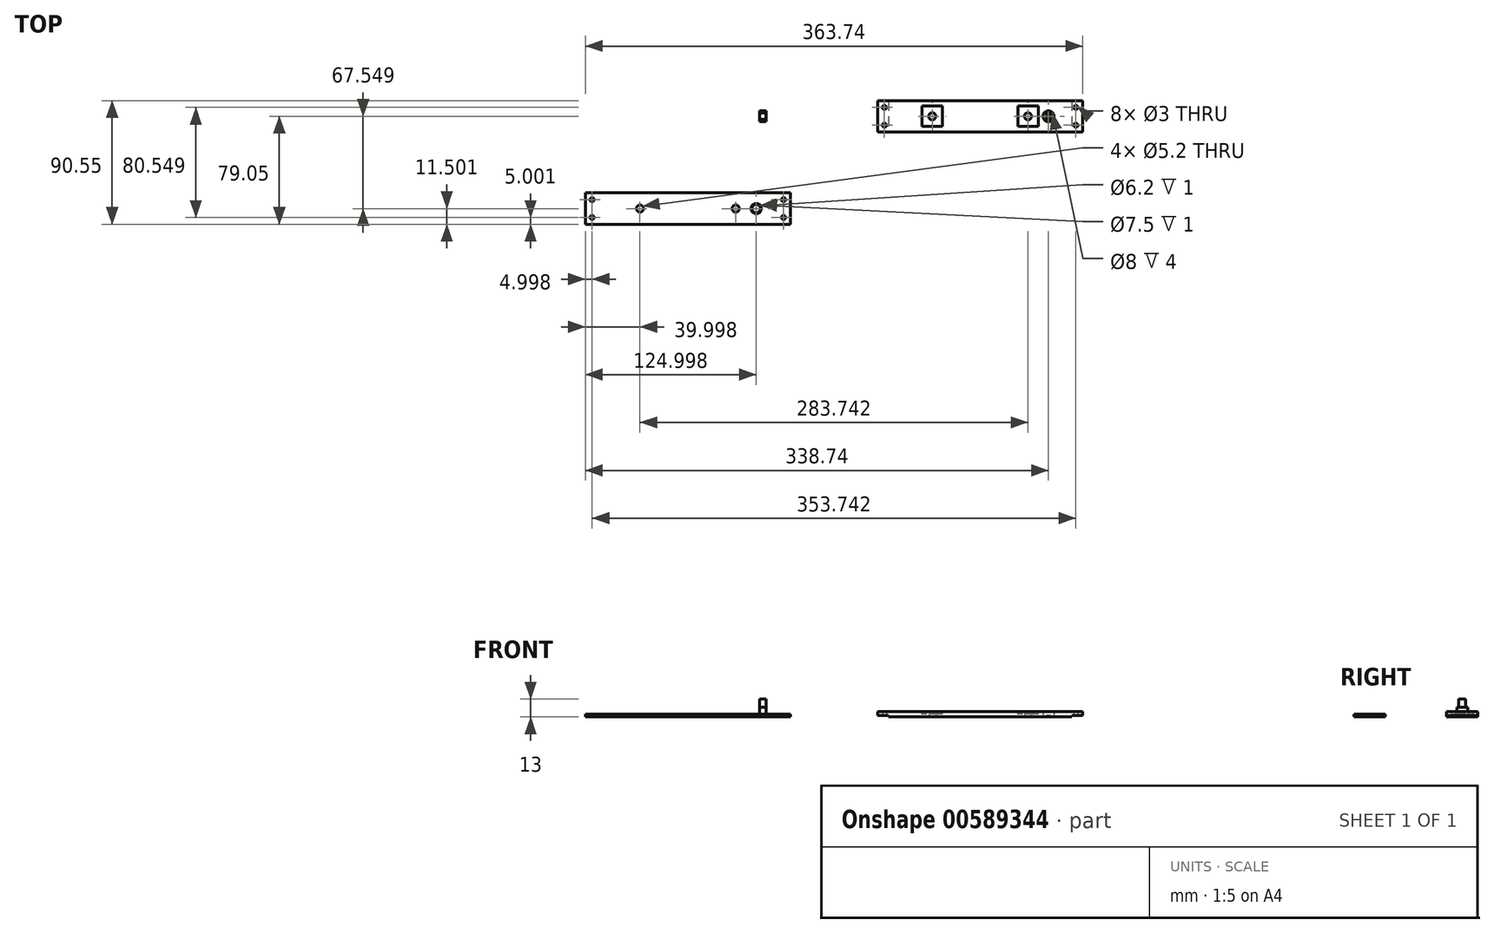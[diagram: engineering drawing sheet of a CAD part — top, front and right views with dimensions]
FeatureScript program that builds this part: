
annotation { "Feature Type Name" : "Feature", "Feature Type Description" : "" }
export const myFeature = defineFeature(function(context is Context, id is Id, definition is map)
    precondition{}
    {
        {
            var Q0;
            Q0=qCreatedBy(makeId("Top.planeOp"),FACE);
            var sketch = newSketch(context, id + "F0", { "sketchPlane" : qUnion([Q0])});
            skLineSegment(sketch, "E0.bottom", {"start": v(75, -11.5) * mm, "end": v(-75, -11.5) * mm});
            skLineSegment(sketch, "E0.top", {"start": v(75, 11.5) * mm, "end": v(-75, 11.5) * mm});
            skLineSegment(sketch, "E0.left", {"start": v(75, -11.5) * mm, "end": v(75, 11.5) * mm});
            skLineSegment(sketch, "E0.right", {"start": v(-75, -11.5) * mm, "end": v(-75, 11.5) * mm});
            skPoint(sketch, "E0.middle", {"position": v(0, 0) * mm});
            skLineSegment(sketch, "E1.bottom", {"start": v(-75, 11.5) * mm, "end": v(-67, 11.5) * mm, "construction": true});
            skLineSegment(sketch, "E1.top", {"start": v(-75, -11.5) * mm, "end": v(-67, -11.5) * mm, "construction": true});
            skLineSegment(sketch, "E1.left", {"start": v(-75, 11.5) * mm, "end": v(-75, -11.5) * mm, "construction": true});
            skLineSegment(sketch, "E1.right", {"start": v(-67, 11.5) * mm, "end": v(-67, -11.5) * mm, "construction": true});
            skLineSegment(sketch, "E2.bottom", {"start": v(75, -11.5) * mm, "end": v(67, -11.5) * mm, "construction": true});
            skLineSegment(sketch, "E2.top", {"start": v(75, 11.5) * mm, "end": v(67, 11.5) * mm, "construction": true});
            skLineSegment(sketch, "E2.left", {"start": v(75, -11.5) * mm, "end": v(75, 11.5) * mm, "construction": true});
            skLineSegment(sketch, "E2.right", {"start": v(67, -11.5) * mm, "end": v(67, 11.5) * mm, "construction": true});
            skCircle(sketch, "E3", {"center": v(-35, 0) * mm, "radius": 2.6 * mm});
            skCircle(sketch, "E4", {"center": v(35, 0) * mm, "radius": 2.6 * mm});
            skCircle(sketch, "E5", {"center": v(50, 0) * mm, "radius": 4 * mm});
            skLineSegment(sketch, "E6.left", {"start": v(51.5, -3.7) * mm, "end": v(51.5, 3.7) * mm});
            skLineSegment(sketch, "E6.right", {"start": v(48.5, -3.7) * mm, "end": v(48.5, 3.7) * mm});
            skCircle(sketch, "E7", {"center": v(-70, 6.5) * mm, "radius": 1.5 * mm});
            skCircle(sketch, "E8", {"center": v(-70, -6.5) * mm, "radius": 1.5 * mm});
            skCircle(sketch, "E9", {"center": v(70, 6.5) * mm, "radius": 1.5 * mm});
            skCircle(sketch, "E10", {"center": v(70, -6.5) * mm, "radius": 1.5 * mm});
            skSolve(sketch);
        }
        {
            var Q0;
            Q0=qCreatedBy(makeId("Top.planeOp"),FACE);
            var sketch = newSketch(context, id + "F1", { "sketchPlane" : qUnion([Q0])});
            skLineSegment(sketch, "E11.bottom", {"start": v(-156.38, -3.9) * mm, "end": v(-161.38, -3.9) * mm});
            skLineSegment(sketch, "E11.top", {"start": v(-156.38, 4.1) * mm, "end": v(-161.38, 4.1) * mm});
            skLineSegment(sketch, "E11.left", {"start": v(-156.38, -3.9) * mm, "end": v(-156.38, 4.1) * mm});
            skLineSegment(sketch, "E11.right", {"start": v(-161.38, -3.9) * mm, "end": v(-161.38, 4.1) * mm});
            skPoint(sketch, "E11.middle", {"position": v(-158.88, 0.1) * mm});
            skSolve(sketch);
        }
        {
            var Q0;
            Q0=makeQuery(id+"F1.imprint","IMPRINT",FACE,{"disambiguationData":[TD([[makeQuery(id+"F1.imprint","IMPRINT",EDGE,{"derivedFrom":sQuery(id+"F1.wireOp",EDGE,"E11.bottom")}),-1.0]])]});
            extrude(context, id + "F2", {"entities" : qUnion([Q0]), "depth" : 7 * mm});
        }
        {
            var Q0;
            Q0=makeQuery(id+"F2.opExtrude","CAP_FACE",FACE,{"disambiguationData":[OSD([sQuery(id+"F1.wireOp",EDGE,"E11.bottom"),sQuery(id+"F1.wireOp",EDGE,"E11.top"),sQuery(id+"F1.wireOp",EDGE,"E11.left"),sQuery(id+"F1.wireOp",EDGE,"E11.right")])],"isStart":false});
            var sketch = newSketch(context, id + "F3", { "sketchPlane" : qUnion([Q0])});
            skCircle(sketch, "E12", {"center": v(-158.88, 0.1) * mm, "radius": 2.5 * mm});
            skPoint(sketch, "E12.centerSnap0", {"position": v(-161.38, 0.1) * mm});
            skPoint(sketch, "E12.centerSnap1", {"position": v(-158.88, 4.1) * mm});
            skSolve(sketch);
        }
        {
            var Q0;
            {var subQ0=sQuery(id+"F3.wireOp",EDGE,"E12");var subQ1=makeQuery(id+"F3.imprint","INTERSECT",VERTEX,{"derivedFrom":[makeQuery(id+"F2.opExtrude","CAP_EDGE",EDGE,{"disambiguationData":[OSD([sQuery(id+"F1.wireOp",EDGE,"E11.left")])],"isStart":false}),subQ0]});Q0=makeQuery(id+"F3.imprint","IMPRINT",FACE,{"disambiguationData":[TD([[makeQuery(id+"F3.imprint","IMPRINT",EDGE,{"disambiguationData":[TD([[subQ1,-1.0]])],"derivedFrom":subQ0}),1.0]])]});}
            extrude(context, id + "F4", {"entities" : qUnion([Q0]), "operationType" : NewBodyOperationType.ADD, "depth" : 6 * mm});
        }
        {
            var Q0;
            Q0=makeQuery(id+"F0.imprint","IMPRINT",FACE,{"disambiguationData":[TD([[makeQuery(id+"F0.imprint","IMPRINT",EDGE,{"derivedFrom":sQuery(id+"F0.wireOp",EDGE,"E0.bottom")}),-1.0]])]});
            var Q1;
            {var subQ0=sQuery(id+"F0.wireOp",EDGE,"E6.left");Q1=makeQuery(id+"F0.imprint","IMPRINT",FACE,{"disambiguationData":[TD([[makeQuery(id+"F0.imprint","IMPRINT",EDGE,{"derivedFrom":subQ0}),1.0]])]});}
            extrude(context, id + "F5", {"entities" : qUnion([Q0, Q1]), "depth" : 4 * mm});
        }
        {
            var Q0;
            Q0=qCreatedBy(makeId("Top.planeOp"),FACE);
            var sketch = newSketch(context, id + "F6", { "sketchPlane" : qUnion([Q0])});
            skLineSegment(sketch, "E13.bottom", {"start": v(-138.74, -79.05) * mm, "end": v(-288.74, -79.05) * mm});
            skLineSegment(sketch, "E13.top", {"start": v(-138.74, -56.05) * mm, "end": v(-288.74, -56.05) * mm});
            skLineSegment(sketch, "E13.left", {"start": v(-138.74, -79.05) * mm, "end": v(-138.74, -56.05) * mm});
            skLineSegment(sketch, "E13.right", {"start": v(-288.74, -79.05) * mm, "end": v(-288.74, -56.05) * mm});
            skPoint(sketch, "E13.middle", {"position": v(-213.74, -67.55) * mm});
            skLineSegment(sketch, "E14.bottom", {"start": v(-288.74, -56.05) * mm, "end": v(-280.74, -56.05) * mm, "construction": true});
            skLineSegment(sketch, "E14.top", {"start": v(-288.74, -79.05) * mm, "end": v(-280.74, -79.05) * mm, "construction": true});
            skLineSegment(sketch, "E14.left", {"start": v(-288.74, -56.05) * mm, "end": v(-288.74, -79.05) * mm, "construction": true});
            skLineSegment(sketch, "E14.right", {"start": v(-280.74, -56.05) * mm, "end": v(-280.74, -79.05) * mm, "construction": true});
            skLineSegment(sketch, "E15.bottom", {"start": v(-138.74, -79.05) * mm, "end": v(-146.74, -79.05) * mm, "construction": true});
            skLineSegment(sketch, "E15.top", {"start": v(-138.74, -56.05) * mm, "end": v(-146.74, -56.05) * mm, "construction": true});
            skLineSegment(sketch, "E15.left", {"start": v(-138.74, -79.05) * mm, "end": v(-138.74, -56.05) * mm, "construction": true});
            skLineSegment(sketch, "E15.right", {"start": v(-146.74, -79.05) * mm, "end": v(-146.74, -56.05) * mm, "construction": true});
            skCircle(sketch, "E16", {"center": v(-248.74, -67.55) * mm, "radius": 2.6 * mm});
            skCircle(sketch, "E17", {"center": v(-178.74, -67.55) * mm, "radius": 2.6 * mm});
            skCircle(sketch, "E18", {"center": v(-163.74, -67.55) * mm, "radius": 3.1 * mm});
            skCircle(sketch, "E19", {"center": v(-283.74, -61.05) * mm, "radius": 1.5 * mm});
            skCircle(sketch, "E20", {"center": v(-283.74, -74.05) * mm, "radius": 1.5 * mm});
            skCircle(sketch, "E21", {"center": v(-143.74, -61.05) * mm, "radius": 1.5 * mm});
            skCircle(sketch, "E22", {"center": v(-143.74, -74.05) * mm, "radius": 1.5 * mm});
            skSolve(sketch);
        }
        {
            var Q0;
            Q0=makeQuery(id+"F6.imprint","IMPRINT",FACE,{"disambiguationData":[TD([[makeQuery(id+"F6.imprint","IMPRINT",EDGE,{"derivedFrom":sQuery(id+"F6.wireOp",EDGE,"E13.bottom")}),-1.0]])]});
            extrude(context, id + "F7", {"entities" : qUnion([Q0]), "depth" : 2 * mm});
        }
        {
            var Q0;
            Q0=makeQuery(id+"F7.opExtrude","CAP_FACE",FACE,{"disambiguationData":[OSD([sQuery(id+"F6.wireOp",EDGE,"E13.bottom"),sQuery(id+"F6.wireOp",EDGE,"E13.top"),sQuery(id+"F6.wireOp",EDGE,"E13.left"),sQuery(id+"F6.wireOp",EDGE,"E13.right"),sQuery(id+"F6.wireOp",EDGE,"E16"),sQuery(id+"F6.wireOp",EDGE,"E17"),sQuery(id+"F6.wireOp",EDGE,"E18")])],"isStart":false});
            var sketch = newSketch(context, id + "F8", { "sketchPlane" : qUnion([Q0])});
            skCircle(sketch, "E23", {"center": v(-163.74, -67.55) * mm, "radius": 3.75 * mm});
            skSolve(sketch);
        }
        {
            var Q0;
            Q0=qSketchRegion(id+"F8",true);
            extrude(context, id + "F9", {"entities" : qUnion([Q0]), "operationType" : NewBodyOperationType.REMOVE, "oppositeDirection" : true, "depth" : 1 * mm});
        }
        {
            var Q0;
            Q0=makeQuery(id+"F5.opExtrude","SWEPT_FACE",FACE,{"disambiguationData":[OSD([sQuery(id+"F0.wireOp",EDGE,"E0.bottom")])]});
            var sketch = newSketch(context, id + "F10", { "sketchPlane" : qUnion([Q0])});
            skLineSegment(sketch, "E24.bottom", {"start": v(-75, 0) * mm, "end": v(-67, 0) * mm});
            skLineSegment(sketch, "E24.top", {"start": v(-75, 1) * mm, "end": v(-67, 1) * mm});
            skLineSegment(sketch, "E24.left", {"start": v(-75, 0) * mm, "end": v(-75, 1) * mm});
            skLineSegment(sketch, "E24.right", {"start": v(-67, 0) * mm, "end": v(-67, 1) * mm});
            skLineSegment(sketch, "E25.bottom", {"start": v(75, 0) * mm, "end": v(67, 0) * mm});
            skLineSegment(sketch, "E25.top", {"start": v(75, 1) * mm, "end": v(67, 1) * mm});
            skLineSegment(sketch, "E25.left", {"start": v(75, 0) * mm, "end": v(75, 1) * mm});
            skLineSegment(sketch, "E25.right", {"start": v(67, 0) * mm, "end": v(67, 1) * mm});
            skSolve(sketch);
        }
        {
            var Q0;
            Q0=qSketchRegion(id+"F10",true);
            extrude(context, id + "F11", {"entities" : qUnion([Q0]), "operationType" : NewBodyOperationType.REMOVE, "oppositeDirection" : true, "depth" : 30 * mm});
        }
        {
            var Q0;
            Q0=makeQuery(id+"F5.opExtrude","CAP_FACE",FACE,{"disambiguationData":[OSD([sQuery(id+"F0.wireOp",EDGE,"E0.bottom"),sQuery(id+"F0.wireOp",EDGE,"E0.top"),sQuery(id+"F0.wireOp",EDGE,"E0.left"),sQuery(id+"F0.wireOp",EDGE,"E0.right"),sQuery(id+"F0.wireOp",EDGE,"E3"),sQuery(id+"F0.wireOp",EDGE,"E4"),sQuery(id+"F0.wireOp",EDGE,"E5")])],"isStart":false});
            var sketch = newSketch(context, id + "F12", { "sketchPlane" : qUnion([Q0])});
            skLineSegment(sketch, "E26.bottom", {"start": v(-27.5, -7.5) * mm, "end": v(-42.5, -7.5) * mm});
            skLineSegment(sketch, "E26.top", {"start": v(-27.5, 7.5) * mm, "end": v(-42.5, 7.5) * mm});
            skLineSegment(sketch, "E26.left", {"start": v(-27.5, -7.5) * mm, "end": v(-27.5, 7.5) * mm});
            skLineSegment(sketch, "E26.right", {"start": v(-42.5, -7.5) * mm, "end": v(-42.5, 7.5) * mm});
            skPoint(sketch, "E26.middle", {"position": v(-35, 0) * mm});
            skLineSegment(sketch, "E27.bottom", {"start": v(42.5, -7.5) * mm, "end": v(27.5, -7.5) * mm});
            skLineSegment(sketch, "E27.top", {"start": v(42.5, 7.5) * mm, "end": v(27.5, 7.5) * mm});
            skLineSegment(sketch, "E27.left", {"start": v(42.5, -7.5) * mm, "end": v(42.5, 7.5) * mm});
            skLineSegment(sketch, "E27.right", {"start": v(27.5, -7.5) * mm, "end": v(27.5, 7.5) * mm});
            skPoint(sketch, "E27.middle", {"position": v(35, 0) * mm});
            skSolve(sketch);
        }
        {
            var Q0;
            Q0=makeQuery(id+"F12.imprint","IMPRINT",FACE,{"disambiguationData":[TD([[makeQuery(id+"F12.imprint","IMPRINT",EDGE,{"derivedFrom":sQuery(id+"F12.wireOp",EDGE,"E26.bottom")}),-1.0]])]});
            var Q1;
            Q1=makeQuery(id+"F12.imprint","IMPRINT",FACE,{"disambiguationData":[TD([[makeQuery(id+"F12.imprint","IMPRINT",EDGE,{"derivedFrom":sQuery(id+"F12.wireOp",EDGE,"E27.bottom")}),-1.0]])]});
            extrude(context, id + "F13", {"entities" : qUnion([Q0, Q1]), "operationType" : NewBodyOperationType.REMOVE, "oppositeDirection" : true, "depth" : 2 * mm});
        }
        {
            var Q0;
            Q0=makeQuery(id+"F5.opExtrude","CAP_FACE",FACE,{"disambiguationData":[OSD([sQuery(id+"F0.wireOp",EDGE,"E0.bottom"),sQuery(id+"F0.wireOp",EDGE,"E0.top"),sQuery(id+"F0.wireOp",EDGE,"E0.left"),sQuery(id+"F0.wireOp",EDGE,"E0.right"),sQuery(id+"F0.wireOp",EDGE,"E3"),sQuery(id+"F0.wireOp",EDGE,"E4"),sQuery(id+"F0.wireOp",EDGE,"E5"),sQuery(id+"F0.wireOp",EDGE,"E6.left"),sQuery(id+"F0.wireOp",EDGE,"E6.right")])],"isStart":false});
            var sketch = newSketch(context, id + "F14", { "sketchPlane" : qUnion([Q0])});
            skCircle(sketch, "E28", {"center": v(50, 0) * mm, "radius": 4 * mm});
            skSolve(sketch);
        }
        {
            var Q0;
            Q0=qSketchRegion(id+"F14",true);
            extrude(context, id + "F15", {"entities" : qUnion([Q0]), "operationType" : NewBodyOperationType.REMOVE, "oppositeDirection" : true, "depth" : 3 * mm});
        }
    });
